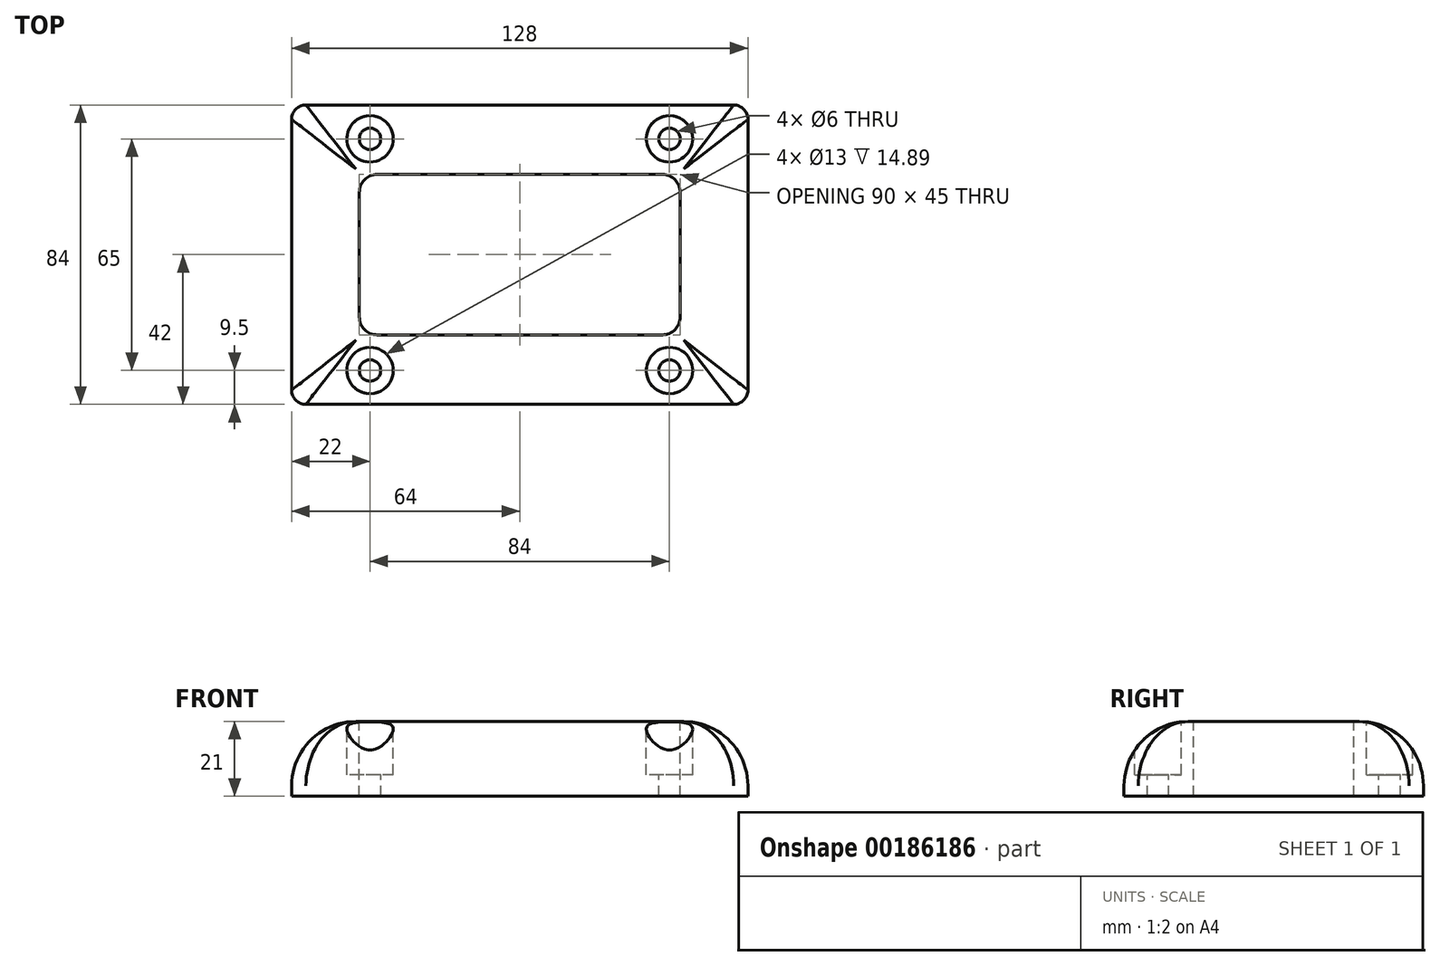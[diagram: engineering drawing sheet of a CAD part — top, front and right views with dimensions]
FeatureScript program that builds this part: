
annotation { "Feature Type Name" : "Feature", "Feature Type Description" : "" }
export const myFeature = defineFeature(function(context is Context, id is Id, definition is map)
    precondition{}
    {
        {
            var Q0;
            Q0=qCreatedBy(makeId("Top.planeOp"),FACE);
            var sketch = newSketch(context, id + "F0", { "sketchPlane" : qUnion([Q0])});
            skLineSegment(sketch, "E0.bottom", {"start": v(64, -42) * mm, "end": v(-64, -42) * mm});
            skLineSegment(sketch, "E0.top", {"start": v(64, 42) * mm, "end": v(-64, 42) * mm});
            skLineSegment(sketch, "E0.left", {"start": v(64, -42) * mm, "end": v(64, 42) * mm});
            skLineSegment(sketch, "E0.right", {"start": v(-64, -42) * mm, "end": v(-64, 42) * mm});
            skPoint(sketch, "E0.middle", {"position": v(0, 0) * mm});
            skSolve(sketch);
        }
        {
            var Q0;
            Q0=makeQuery(id+"F0.imprint","IMPRINT",FACE,{"disambiguationData":[TD([[makeQuery(id+"F0.imprint","IMPRINT",EDGE,{"derivedFrom":sQuery(id+"F0.wireOp",EDGE,"E0.bottom")}),-1.0]])]});
            var Q1;
            Q1 = qSketchRegion(id + "F2", true);
            extrude(context, id + "F1", {"entities" : qUnion([Q0, Q1]), "depth" : 21 * mm});
        }
        {
            var Q0;
            Q0=makeQuery(id+"F1.opExtrude","CAP_FACE",FACE,{"disambiguationData":[OSD([sQuery(id+"F0.wireOp",EDGE,"E0.bottom"),sQuery(id+"F0.wireOp",EDGE,"E0.top"),sQuery(id+"F0.wireOp",EDGE,"E0.left"),sQuery(id+"F0.wireOp",EDGE,"E0.right")])],"isStart":false});
            var sketch = newSketch(context, id + "F2", { "sketchPlane" : qUnion([Q0])});
            skLineSegment(sketch, "E1.bottom", {"start": v(42, -32.5) * mm, "end": v(-42, -32.5) * mm});
            skLineSegment(sketch, "E1.top", {"start": v(42, 32.5) * mm, "end": v(-42, 32.5) * mm});
            skLineSegment(sketch, "E1.left", {"start": v(42, -32.5) * mm, "end": v(42, 32.5) * mm});
            skLineSegment(sketch, "E1.right", {"start": v(-42, -32.5) * mm, "end": v(-42, 32.5) * mm});
            skPoint(sketch, "E1.middle", {"position": v(0, 0) * mm});
            skSolve(sketch);
        }
        {
            var Q0;
            Q0=sQuery(id+"F2.wireOp",VERTEX,"E1.right.start");
            var Q1;
            Q1=sQuery(id+"F2.wireOp",VERTEX,"E1.top.end");
            var Q2;
            Q2=sQuery(id+"F2.wireOp",VERTEX,"E1.left.end");
            var Q3;
            Q3=sQuery(id+"F2.wireOp",VERTEX,"E1.left.start");
            var Q4;
            Q4=makeQuery(id+"F1.opExtrude","SWEPT_BODY",BODY,{"disambiguationData":[OSD([sQuery(id+"F0.wireOp",EDGE,"E0.bottom"),sQuery(id+"F0.wireOp",EDGE,"E0.top"),sQuery(id+"F0.wireOp",EDGE,"E0.left"),sQuery(id+"F0.wireOp",EDGE,"E0.right")])]});
            hole(context, id + "F3", {"style" : HoleStyle.C_BORE, "endStyle" : HoleEndStyle.THROUGH, "holeDiameter" : 6 * mm, "cBoreDiameter" : 13 * mm, "cBoreDepth" : 15 * mm, "startFromSketch" : true, "locations" : qUnion([Q0, Q1, Q2, Q3]), "scope" : qUnion([Q4]), "isTappedThrough" : true});
        }
        {
            var Q0;
            Q0=makeQuery(id+"F1.opExtrude","CAP_EDGE",EDGE,{"disambiguationData":[OSD([sQuery(id+"F0.wireOp",EDGE,"E0.bottom")])],"isStart":false});
            var Q1;
            Q1=makeQuery(id+"F1.opExtrude","CAP_EDGE",EDGE,{"disambiguationData":[OSD([sQuery(id+"F0.wireOp",EDGE,"E0.left")])],"isStart":false});
            var Q2;
            Q2=makeQuery(id+"F1.opExtrude","CAP_EDGE",EDGE,{"disambiguationData":[OSD([sQuery(id+"F0.wireOp",EDGE,"E0.top")])],"isStart":false});
            var Q3;
            Q3=makeQuery(id+"F1.opExtrude","CAP_EDGE",EDGE,{"disambiguationData":[OSD([sQuery(id+"F0.wireOp",EDGE,"E0.right")])],"isStart":false});
            fillet(context, id + "F4", {"entities" : qUnion([Q0, Q1, Q2, Q3]), "radius" : 18 * mm, "tangentPropagation" : true, "allowEdgeOverflow" : false});
        }
        {
            var Q0;
            Q0=makeQuery(id+"F1.opExtrude","CAP_FACE",FACE,{"disambiguationData":[OSD([sQuery(id+"F0.wireOp",EDGE,"E0.bottom"),sQuery(id+"F0.wireOp",EDGE,"E0.top"),sQuery(id+"F0.wireOp",EDGE,"E0.left"),sQuery(id+"F0.wireOp",EDGE,"E0.right")])],"isStart":false});
            var sketch = newSketch(context, id + "F5", { "sketchPlane" : qUnion([Q0])});
            skLineSegment(sketch, "E2.bottom", {"start": v(45, 22.5) * mm, "end": v(-45, 22.5) * mm});
            skLineSegment(sketch, "E2.top", {"start": v(45, -22.5) * mm, "end": v(-45, -22.5) * mm});
            skLineSegment(sketch, "E2.left", {"start": v(45, 22.5) * mm, "end": v(45, -22.5) * mm});
            skLineSegment(sketch, "E2.right", {"start": v(-45, 22.5) * mm, "end": v(-45, -22.5) * mm});
            skPoint(sketch, "E2.middle", {"position": v(0, 0) * mm});
            skSolve(sketch);
        }
        {
            var Q0;
            Q0 = qSketchRegion(id + "F5", true);
            extrude(context, id + "F6", {"entities" : qUnion([Q0]), "operationType" : NewBodyOperationType.REMOVE, "endBound" : BoundingType.THROUGH_ALL, "oppositeDirection" : true, "depth" : 25 * mm});
        }
        {
            var Q0;
            Q0=makeQuery(id+"F6.boolean.opBoolean","COPY",EDGE,{"derivedFrom":makeQuery(id+"F6.opExtrude","SWEPT_EDGE",EDGE,{"disambiguationData":[OSD([sQuery(id+"F5.wireOp",EDGE,"E2.bottom"),sQuery(id+"F5.wireOp",EDGE,"E2.right")])]})});
            var Q1;
            Q1=makeQuery(id+"F6.boolean.opBoolean","COPY",EDGE,{"derivedFrom":makeQuery(id+"F6.opExtrude","SWEPT_EDGE",EDGE,{"disambiguationData":[OSD([sQuery(id+"F5.wireOp",EDGE,"E2.top"),sQuery(id+"F5.wireOp",EDGE,"E2.right")])]})});
            var Q2;
            Q2=makeQuery(id+"F6.boolean.opBoolean","COPY",EDGE,{"derivedFrom":makeQuery(id+"F6.opExtrude","SWEPT_EDGE",EDGE,{"disambiguationData":[OSD([sQuery(id+"F5.wireOp",EDGE,"E2.top"),sQuery(id+"F5.wireOp",EDGE,"E2.left")])]})});
            var Q3;
            Q3=makeQuery(id+"F6.boolean.opBoolean","COPY",EDGE,{"derivedFrom":makeQuery(id+"F6.opExtrude","SWEPT_EDGE",EDGE,{"disambiguationData":[OSD([sQuery(id+"F5.wireOp",EDGE,"E2.bottom"),sQuery(id+"F5.wireOp",EDGE,"E2.left")])]})});
            fillet(context, id + "F7", {"entities" : qUnion([Q0, Q1, Q2, Q3]), "radius" : 5 * mm, "tangentPropagation" : true, "allowEdgeOverflow" : false});
        }
        {
            var Q0;
            Q0=makeQuery(id+"F4.opFillet","BLEND_EDGE",EDGE,{"blendedFrom":[makeQuery(id+"F1.opExtrude","CAP_EDGE",EDGE,{"disambiguationData":[OSD([sQuery(id+"F0.wireOp",EDGE,"E0.bottom")])],"isStart":false}),makeQuery(id+"F1.opExtrude","CAP_EDGE",EDGE,{"disambiguationData":[OSD([sQuery(id+"F0.wireOp",EDGE,"E0.left")])],"isStart":false})],"blendedInto":[]});
            var Q1;
            Q1=makeQuery(id+"F4.opFillet","BLEND_EDGE",EDGE,{"blendedFrom":[makeQuery(id+"F1.opExtrude","CAP_EDGE",EDGE,{"disambiguationData":[OSD([sQuery(id+"F0.wireOp",EDGE,"E0.top")])],"isStart":false}),makeQuery(id+"F1.opExtrude","CAP_EDGE",EDGE,{"disambiguationData":[OSD([sQuery(id+"F0.wireOp",EDGE,"E0.left")])],"isStart":false})],"blendedInto":[]});
            var Q2;
            Q2=makeQuery(id+"F4.opFillet","BLEND_EDGE",EDGE,{"blendedFrom":[makeQuery(id+"F1.opExtrude","CAP_EDGE",EDGE,{"disambiguationData":[OSD([sQuery(id+"F0.wireOp",EDGE,"E0.top")])],"isStart":false}),makeQuery(id+"F1.opExtrude","CAP_EDGE",EDGE,{"disambiguationData":[OSD([sQuery(id+"F0.wireOp",EDGE,"E0.right")])],"isStart":false})],"blendedInto":[]});
            var Q3;
            Q3=makeQuery(id+"F4.opFillet","BLEND_EDGE",EDGE,{"blendedFrom":[makeQuery(id+"F1.opExtrude","CAP_EDGE",EDGE,{"disambiguationData":[OSD([sQuery(id+"F0.wireOp",EDGE,"E0.bottom")])],"isStart":false}),makeQuery(id+"F1.opExtrude","CAP_EDGE",EDGE,{"disambiguationData":[OSD([sQuery(id+"F0.wireOp",EDGE,"E0.right")])],"isStart":false})],"blendedInto":[]});
            fillet(context, id + "F8", {"entities" : qUnion([Q0, Q1, Q2, Q3]), "radius" : 4 * mm, "tangentPropagation" : true, "allowEdgeOverflow" : false});
        }
    });
